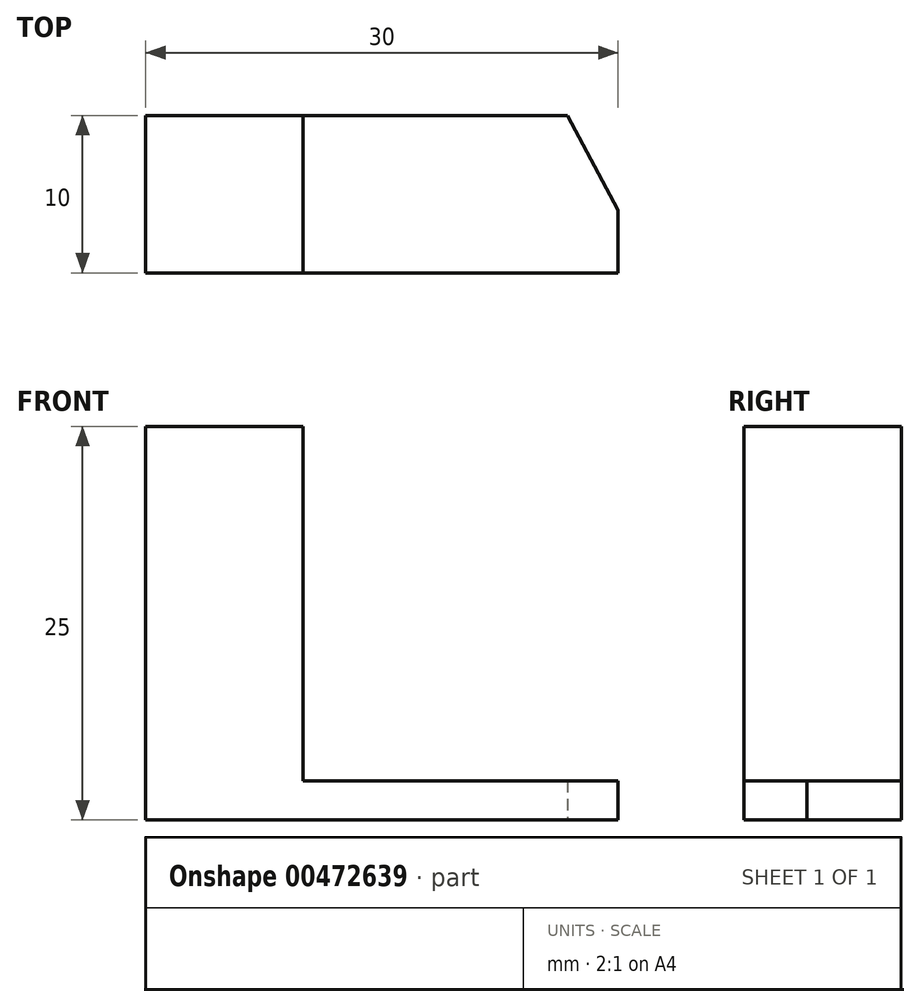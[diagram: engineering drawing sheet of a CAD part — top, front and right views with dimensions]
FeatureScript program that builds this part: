
annotation { "Feature Type Name" : "Feature", "Feature Type Description" : "" }
export const myFeature = defineFeature(function(context is Context, id is Id, definition is map)
    precondition{}
    {
        {
            var Q0;
            Q0=qCreatedBy(makeId("Top.planeOp"),FACE);
            var sketch = newSketch(context, id + "F0", { "sketchPlane" : qUnion([Q0])});
            skLineSegment(sketch, "E0.bottom", {"start": v(-1.25, -2.7) * mm, "end": v(-31.25, -2.7) * mm});
            skLineSegment(sketch, "E0.top", {"start": v(-4.47, 7.3) * mm, "end": v(-31.25, 7.3) * mm});
            skLineSegment(sketch, "E0.left", {"start": v(-1.25, -2.7) * mm, "end": v(-1.25, 1.3) * mm});
            skLineSegment(sketch, "E0.right", {"start": v(-31.25, -2.7) * mm, "end": v(-31.25, 7.3) * mm});
            skLineSegment(sketch, "E1", {"start": v(-4.47, 7.3) * mm, "end": v(-1.25, 1.3) * mm});
            skLineSegment(sketch, "E2", {"start": v(-21.25, 7.3) * mm, "end": v(-21.25, -2.7) * mm});
            skSolve(sketch);
        }
        {
            var Q0;
            Q0 = qSketchRegion(id + "F0", true);
            extrude(context, id + "F1", {"entities" : qUnion([Q0]), "depth" : 2.5 * mm});
        }
        {
            var Q0;
            {var subQ0=sQuery(id+"F0.wireOp",EDGE,"E0.right");Q0=makeQuery(id+"F0.imprint","IMPRINT",FACE,{"disambiguationData":[TD([[makeQuery(id+"F0.imprint","IMPRINT",EDGE,{"derivedFrom":subQ0}),-1.0]])]});}
            extrude(context, id + "F2", {"entities" : qUnion([Q0]), "operationType" : NewBodyOperationType.ADD, "depth" : 25 * mm});
        }
    });
